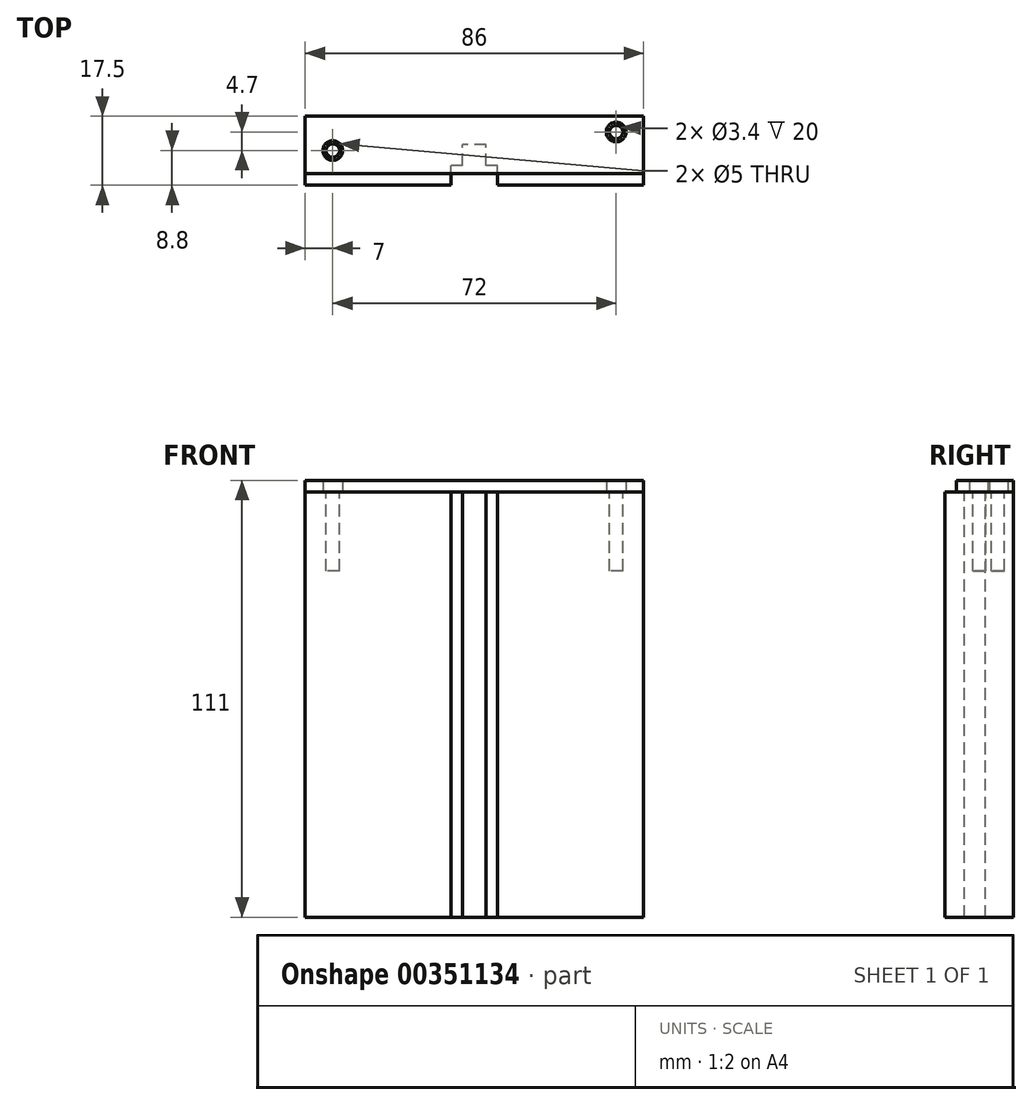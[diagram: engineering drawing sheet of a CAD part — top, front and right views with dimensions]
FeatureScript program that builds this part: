
annotation { "Feature Type Name" : "Feature", "Feature Type Description" : "" }
export const myFeature = defineFeature(function(context is Context, id is Id, definition is map)
    precondition{}
    {
        {
            var Q0;
            Q0=qCreatedBy(makeId("Top.planeOp"),FACE);
            var sketch = newSketch(context, id + "F0", { "sketchPlane" : qUnion([Q0])});
            skLineSegment(sketch, "E0.bottom", {"start": v(43, -7.25) * mm, "end": v(-43, -7.25) * mm});
            skLineSegment(sketch, "E0.top", {"start": v(43, 7.25) * mm, "end": v(-43, 7.25) * mm});
            skLineSegment(sketch, "E0.left", {"start": v(43, -7.25) * mm, "end": v(43, 7.25) * mm});
            skLineSegment(sketch, "E0.right", {"start": v(-43, -7.25) * mm, "end": v(-43, 7.25) * mm});
            skPoint(sketch, "E0.middle", {"position": v(0, 0) * mm});
            skCircle(sketch, "E1", {"center": v(-36, -1.45) * mm, "radius": 2.5 * mm});
            skCircle(sketch, "E2", {"center": v(36, 3.25) * mm, "radius": 2.5 * mm});
            skLineSegment(sketch, "E3.top", {"start": v(43, -10.25) * mm, "end": v(-43, -10.25) * mm});
            skLineSegment(sketch, "E3.left", {"start": v(43, -7.25) * mm, "end": v(43, -10.25) * mm});
            skLineSegment(sketch, "E3.right", {"start": v(-43, -7.25) * mm, "end": v(-43, -10.25) * mm});
            skLineSegment(sketch, "E4.bottom", {"start": v(5.9, -15.25) * mm, "end": v(-5.9, -15.25) * mm});
            skLineSegment(sketch, "E4.top", {"start": v(5.9, -5.25) * mm, "end": v(-5.9, -5.25) * mm});
            skLineSegment(sketch, "E4.left", {"start": v(5.9, -15.25) * mm, "end": v(5.9, -5.25) * mm});
            skLineSegment(sketch, "E4.right", {"start": v(-5.9, -15.25) * mm, "end": v(-5.9, -5.25) * mm});
            skPoint(sketch, "E4.middle", {"position": v(0, -10.25) * mm});
            skLineSegment(sketch, "E5.bottom", {"start": v(3, -20.55) * mm, "end": v(-3, -20.55) * mm});
            skLineSegment(sketch, "E5.top", {"start": v(3, 0.05) * mm, "end": v(-3, 0.05) * mm});
            skLineSegment(sketch, "E5.left", {"start": v(3, -20.55) * mm, "end": v(3, 0.05) * mm});
            skLineSegment(sketch, "E5.right", {"start": v(-3, -20.55) * mm, "end": v(-3, 0.05) * mm});
            skCircle(sketch, "E6", {"center": v(36, 3.25) * mm, "radius": 1.7 * mm});
            skCircle(sketch, "E7", {"center": v(-36, -1.45) * mm, "radius": 1.7 * mm});
            skSolve(sketch);
        }
        {
            var Q0;
            Q0=makeQuery(id+"F0.imprint","IMPRINT",FACE,{"disambiguationData":[TD([[makeQuery(id+"F0.imprint","IMPRINT",EDGE,{"derivedFrom":sQuery(id+"F0.wireOp",EDGE,"E0.top")}),1.0]])]});
            var Q1;
            {var subQ0=sQuery(id+"F0.wireOp",EDGE,"E5.right");var subQ1=sQuery(id+"F0.wireOp",EDGE,"E0.bottom");var subQ2=makeQuery(id+"F0.imprint","INTERSECT",VERTEX,{"derivedFrom":[subQ1,subQ0]});Q1=makeQuery(id+"F0.imprint","IMPRINT",FACE,{"disambiguationData":[TD([[makeQuery(id+"F0.imprint","IMPRINT",EDGE,{"disambiguationData":[TD([[subQ2,-1.0]])],"derivedFrom":subQ1}),-1.0]])]});}
            var Q2;
            {var subQ0=sQuery(id+"F0.wireOp",EDGE,"E5.left");var subQ1=sQuery(id+"F0.wireOp",EDGE,"E0.bottom");var subQ2=makeQuery(id+"F0.imprint","INTERSECT",VERTEX,{"derivedFrom":[subQ1,subQ0]});Q2=makeQuery(id+"F0.imprint","IMPRINT",FACE,{"disambiguationData":[TD([[makeQuery(id+"F0.imprint","IMPRINT",EDGE,{"disambiguationData":[TD([[subQ2,-1.0]])],"derivedFrom":subQ1}),-1.0]])]});}
            var Q3;
            {var subQ5=sQuery(id+"F0.wireOp",EDGE,"E5.top");Q3=makeQuery(id+"F0.imprint","IMPRINT",FACE,{"disambiguationData":[TD([[makeQuery(id+"F0.imprint","IMPRINT",EDGE,{"derivedFrom":subQ5}),1.0]])]});}
            var Q4;
            {var subQ0=sQuery(id+"F0.wireOp",EDGE,"E4.left");var subQ1=sQuery(id+"F0.wireOp",EDGE,"E0.bottom");var subQ2=makeQuery(id+"F0.imprint","INTERSECT",VERTEX,{"derivedFrom":[subQ1,subQ0]});Q4=makeQuery(id+"F0.imprint","IMPRINT",FACE,{"disambiguationData":[TD([[makeQuery(id+"F0.imprint","IMPRINT",EDGE,{"disambiguationData":[TD([[subQ2,-1.0]])],"derivedFrom":subQ1}),-1.0]])]});}
            extrude(context, id + "F1", {"entities" : qUnion([Q0, Q1, Q2, Q3, Q4]), "depth" : 3 * mm});
        }
        {
            var Q0;
            Q0=makeQuery(id+"F0.imprint","IMPRINT",FACE,{"disambiguationData":[TD([[makeQuery(id+"F0.imprint","IMPRINT",EDGE,{"derivedFrom":sQuery(id+"F0.wireOp",EDGE,"E0.top")}),1.0]])]});
            var Q1;
            {var subQ0=sQuery(id+"F0.wireOp",EDGE,"E3.right");Q1=makeQuery(id+"F0.imprint","IMPRINT",FACE,{"disambiguationData":[TD([[makeQuery(id+"F0.imprint","IMPRINT",EDGE,{"derivedFrom":subQ0}),1.0]])]});}
            var Q2;
            {var subQ0=sQuery(id+"F0.wireOp",EDGE,"E3.left");Q2=makeQuery(id+"F0.imprint","IMPRINT",FACE,{"disambiguationData":[TD([[makeQuery(id+"F0.imprint","IMPRINT",EDGE,{"derivedFrom":subQ0}),-1.0]])]});}
            var Q3;
            Q3=makeQuery(id+"F0.imprint","IMPRINT",FACE,{"disambiguationData":[TD([[makeQuery(id+"F0.imprint","IMPRINT",EDGE,{"derivedFrom":sQuery(id+"F0.wireOp",EDGE,"E1")}),1.0]])]});
            var Q4;
            Q4=makeQuery(id+"F0.imprint","IMPRINT",FACE,{"disambiguationData":[TD([[makeQuery(id+"F0.imprint","IMPRINT",EDGE,{"derivedFrom":sQuery(id+"F0.wireOp",EDGE,"E6")}),1.0]])]});
            var Q5;
            Q5=makeQuery(id+"F0.imprint","IMPRINT",FACE,{"disambiguationData":[TD([[makeQuery(id+"F0.imprint","IMPRINT",EDGE,{"derivedFrom":sQuery(id+"F0.wireOp",EDGE,"E2")}),1.0]])]});
            var Q6;
            Q6=makeQuery(id+"F0.imprint","IMPRINT",FACE,{"disambiguationData":[TD([[makeQuery(id+"F0.imprint","IMPRINT",EDGE,{"derivedFrom":sQuery(id+"F0.wireOp",EDGE,"E7")}),1.0]])]});
            extrude(context, id + "F2", {"entities" : qUnion([Q0, Q1, Q2, Q3, Q4, Q5, Q6]), "oppositeDirection" : true, "depth" : 108 * mm});
        }
        {
            var Q0;
            Q0=makeQuery(id+"F0.imprint","IMPRINT",FACE,{"disambiguationData":[TD([[makeQuery(id+"F0.imprint","IMPRINT",EDGE,{"derivedFrom":sQuery(id+"F0.wireOp",EDGE,"E7")}),1.0]])]});
            var Q1;
            Q1=makeQuery(id+"F0.imprint","IMPRINT",FACE,{"disambiguationData":[TD([[makeQuery(id+"F0.imprint","IMPRINT",EDGE,{"derivedFrom":sQuery(id+"F0.wireOp",EDGE,"E6")}),1.0]])]});
            extrude(context, id + "F3", {"entities" : qUnion([Q0, Q1]), "operationType" : NewBodyOperationType.REMOVE, "oppositeDirection" : true, "depth" : 20 * mm});
        }
    });
